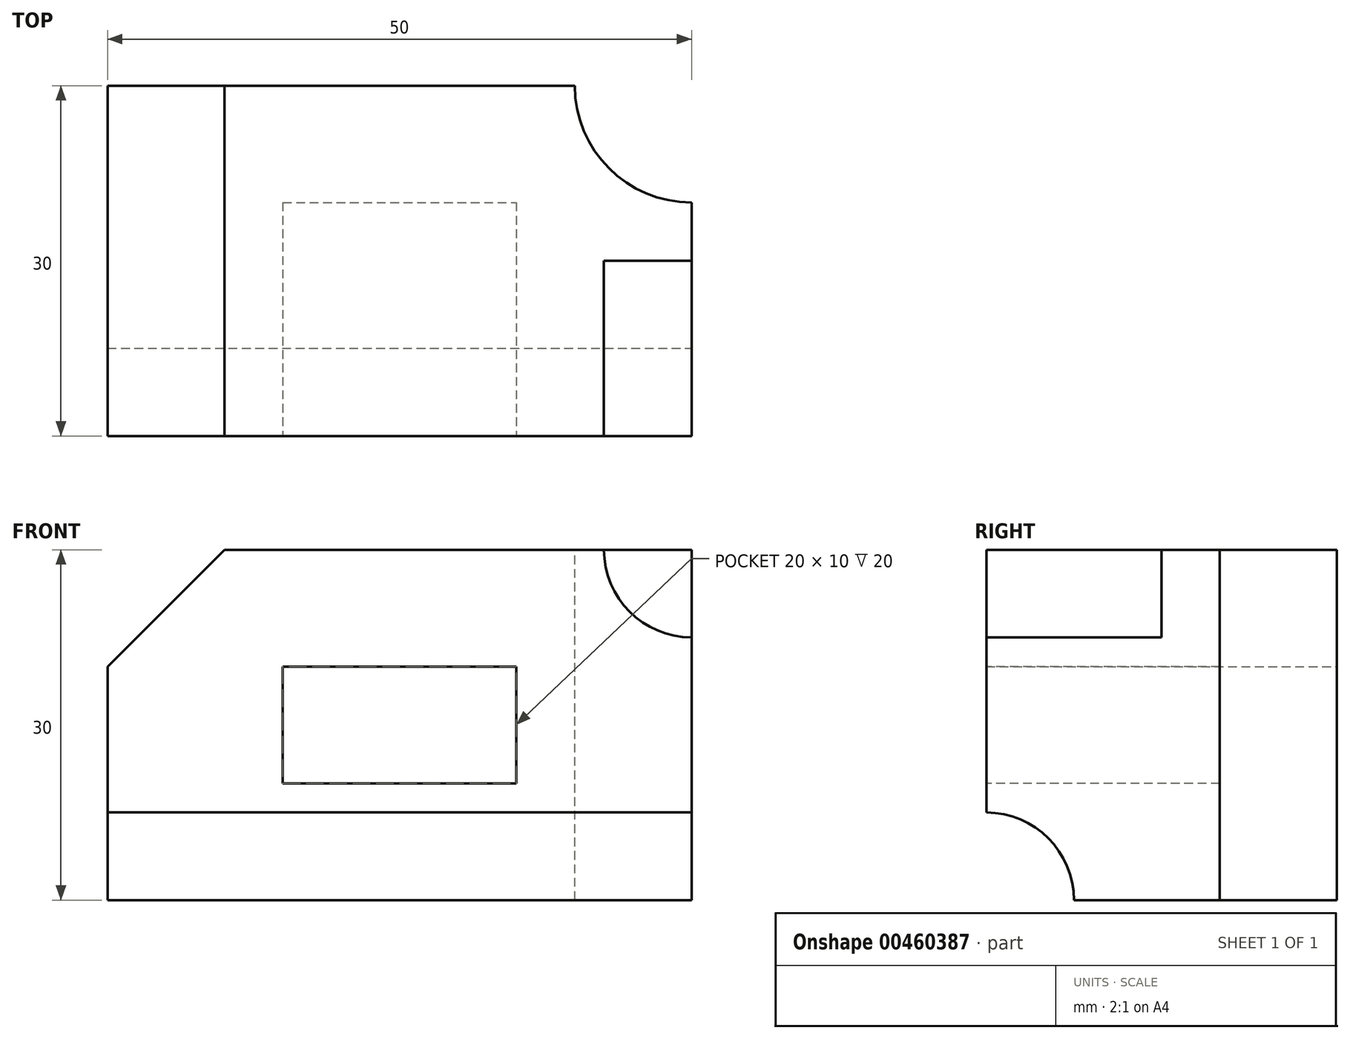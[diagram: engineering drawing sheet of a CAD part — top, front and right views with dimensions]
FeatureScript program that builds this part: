
annotation { "Feature Type Name" : "Feature", "Feature Type Description" : "" }
export const myFeature = defineFeature(function(context is Context, id is Id, definition is map)
    precondition{}
    {
        {
            var Q0;
            Q0=qCreatedBy(makeId("Front.planeOp"),FACE);
            var sketch = newSketch(context, id + "F0", { "sketchPlane" : qUnion([Q0])});
            skLineSegment(sketch, "E0.bottom", {"start": v(0, 0) * mm, "end": v(-50, 0) * mm});
            skLineSegment(sketch, "E0.top", {"start": v(0, 30) * mm, "end": v(-50, 30) * mm});
            skLineSegment(sketch, "E0.left", {"start": v(0, 0) * mm, "end": v(0, 30) * mm});
            skLineSegment(sketch, "E0.right", {"start": v(-50, 0) * mm, "end": v(-50, 30) * mm});
            skLineSegment(sketch, "E1", {"start": v(-50, 30) * mm, "end": v(-40, 30) * mm});
            skLineSegment(sketch, "E2", {"start": v(-40, 30) * mm, "end": v(-50, 20) * mm});
            skLineSegment(sketch, "E3", {"start": v(-50, 20) * mm, "end": v(-50, 30) * mm});
            skSolve(sketch);
        }
        {
            var Q0;
            Q0=makeQuery(id+"F0.imprint","IMPRINT",FACE,{"disambiguationData":[TD([[makeQuery(id+"F0.imprint","IMPRINT",EDGE,{"derivedFrom":sQuery(id+"F0.wireOp",EDGE,"E0.bottom")}),-1.0]])]});
            extrude(context, id + "F1", {"entities" : qUnion([Q0]), "depth" : 30 * mm});
        }
        {
            var Q0;
            Q0=makeQuery(id+"F1.opExtrude","CAP_FACE",FACE,{"disambiguationData":[OSD([sQuery(id+"F0.wireOp",EDGE,"E0.bottom"),sQuery(id+"F0.wireOp",EDGE,"E0.top"),sQuery(id+"F0.wireOp",EDGE,"E0.left"),sQuery(id+"F0.wireOp",EDGE,"E0.right"),sQuery(id+"F0.wireOp",EDGE,"E2")])],"isStart":false});
            var sketch = newSketch(context, id + "F2", { "sketchPlane" : qUnion([Q0])});
            skLineSegment(sketch, "E4.bottom", {"start": v(-35, 20) * mm, "end": v(-15, 20) * mm});
            skLineSegment(sketch, "E4.top", {"start": v(-35, 10) * mm, "end": v(-15, 10) * mm});
            skLineSegment(sketch, "E4.left", {"start": v(-35, 20) * mm, "end": v(-35, 10) * mm});
            skLineSegment(sketch, "E4.right", {"start": v(-15, 20) * mm, "end": v(-15, 10) * mm});
            skSolve(sketch);
        }
        {
            var Q0;
            Q0=makeQuery(id+"F2.imprint","IMPRINT",FACE,{"disambiguationData":[TD([[makeQuery(id+"F2.imprint","IMPRINT",EDGE,{"derivedFrom":sQuery(id+"F2.wireOp",EDGE,"E4.bottom")}),-1.0]])]});
            extrude(context, id + "F3", {"entities" : qUnion([Q0]), "operationType" : NewBodyOperationType.REMOVE, "oppositeDirection" : true, "depth" : 20 * mm});
        }
        {
            var Q0;
            Q0=makeQuery(id+"F1.opExtrude","CAP_FACE",FACE,{"disambiguationData":[OSD([sQuery(id+"F0.wireOp",EDGE,"E0.bottom"),sQuery(id+"F0.wireOp",EDGE,"E0.top"),sQuery(id+"F0.wireOp",EDGE,"E0.left"),sQuery(id+"F0.wireOp",EDGE,"E0.right"),sQuery(id+"F0.wireOp",EDGE,"E2")])],"isStart":false});
            var sketch = newSketch(context, id + "F4", { "sketchPlane" : qUnion([Q0])});
            skCircle(sketch, "E5", {"center": v(0, 30) * mm, "radius": 7.5 * mm});
            skSolve(sketch);
        }
        {
            var Q0;
            {var subQ0=sQuery(id+"F4.wireOp",EDGE,"E5");var subQ1=makeQuery(id+"F1.opExtrude","CAP_EDGE",EDGE,{"disambiguationData":[OSD([sQuery(id+"F0.wireOp",EDGE,"E0.top")])],"isStart":false});var subQ2=makeQuery(id+"F4.imprint","INTERSECT",VERTEX,{"derivedFrom":[subQ1,subQ0]});Q0=makeQuery(id+"F4.imprint","IMPRINT",FACE,{"disambiguationData":[TD([[makeQuery(id+"F4.imprint","IMPRINT",EDGE,{"disambiguationData":[TD([[subQ2,-1.0]])],"derivedFrom":subQ0}),1.0]])]});}
            extrude(context, id + "F5", {"entities" : qUnion([Q0]), "operationType" : NewBodyOperationType.REMOVE, "oppositeDirection" : true, "depth" : 15 * mm});
        }
        {
            var Q0;
            Q0=makeQuery(id+"F1.opExtrude","SWEPT_FACE",FACE,{"disambiguationData":[OSD([sQuery(id+"F0.wireOp",EDGE,"E0.left")])]});
            var sketch = newSketch(context, id + "F6", { "sketchPlane" : qUnion([Q0])});
            skCircle(sketch, "E6", {"center": v(-30, 0) * mm, "radius": 7.5 * mm});
            skSolve(sketch);
        }
        {
            var Q0;
            {var subQ0=sQuery(id+"F6.wireOp",EDGE,"E6");var subQ1=sQuery(id+"F0.wireOp",EDGE,"E0.left");var subQ4=makeQuery(id+"F1.opExtrude","CAP_EDGE",EDGE,{"disambiguationData":[OSD([subQ1])],"isStart":false});var subQ5=makeQuery(id+"F6.imprint","INTERSECT",VERTEX,{"derivedFrom":[subQ4,subQ0]});Q0=makeQuery(id+"F6.imprint","IMPRINT",FACE,{"disambiguationData":[TD([[makeQuery(id+"F6.imprint","IMPRINT",EDGE,{"disambiguationData":[TD([[subQ5,1.0]])],"derivedFrom":subQ0}),1.0]])]});}
            extrude(context, id + "F7", {"entities" : qUnion([Q0]), "operationType" : NewBodyOperationType.REMOVE, "endBound" : BoundingType.THROUGH_ALL, "oppositeDirection" : true, "depth" : 25 * mm});
        }
        {
            var Q0;
            Q0=makeQuery(id+"F1.opExtrude","SWEPT_FACE",FACE,{"disambiguationData":[OSD([sQuery(id+"F0.wireOp",EDGE,"E0.top")])]});
            var sketch = newSketch(context, id + "F8", { "sketchPlane" : qUnion([Q0])});
            skCircle(sketch, "E7", {"center": v(0, 0) * mm, "radius": 10 * mm});
            skSolve(sketch);
        }
        {
            var Q0;
            {var subQ0=sQuery(id+"F8.wireOp",EDGE,"E7");var subQ1=sQuery(id+"F0.wireOp",EDGE,"E0.top");var subQ2=makeQuery(id+"F1.opExtrude","CAP_EDGE",EDGE,{"disambiguationData":[OSD([subQ1])],"isStart":true});var subQ3=makeQuery(id+"F8.imprint","INTERSECT",VERTEX,{"derivedFrom":[subQ2,subQ0]});Q0=makeQuery(id+"F8.imprint","IMPRINT",FACE,{"disambiguationData":[TD([[makeQuery(id+"F8.imprint","IMPRINT",EDGE,{"disambiguationData":[TD([[subQ3,-1.0]])],"derivedFrom":subQ0}),1.0]])]});}
            extrude(context, id + "F9", {"entities" : qUnion([Q0]), "operationType" : NewBodyOperationType.REMOVE, "endBound" : BoundingType.THROUGH_ALL, "oppositeDirection" : true, "depth" : 25 * mm});
        }
    });
